# Revit family: Hardware_Glass_Nero
name_source: partatom
category: Specialty Equipment
units: mm (PartAtom-declared; Revit-internal decimal feet)

## family parameters
Always vertical = Yes
Cut with Voids When Loaded = Yes
OmniClass Number = 23.31.25.00
OmniClass Title = Toilet and Bath Specialties
Part Type = Normal
Room Calculation Point = No
Round Connector Dimension = Use Diameter
Shared = No
Work Plane-Based = No

## types (18) — shared parameters
Assembly Code = C1030210
IfcExportAs = IfcFurniture
IfcExportType = NOTDEFINED
Manufacturer = Nero
ManufacturerURLProductSpecific = https://nerotapware.com.au
ModifiedIssue = 20231106 $
URL = https://nerotapware.com.au
Uniclass2015Code = Pr_30_36_36
Uniclass2015Title = Hinges and hanging hardware
Uniclass2015Version = Products v1.28
zero-valued in all types: Default Elevation

## per-type parameters (varying)
| type | 180DegWallToGlassHinge | 90DegWallHinge | 90DegWallToGlassHinge | BodyMaterial | Description | GapBetweenWallandGlass | GlassPanel | GlassToWallHingeF | GlassToWallHingeU | GlassTopHingeF | GrabRail | ManufacturerSpecCode | Model | PerpendicularGlassLeft | PerpendicularWallLeft | PerpendicularWallThickness | RoundShowerKnob | SquareShowerKnob | Type Comments |
| F Shaped Glass to Wall Bracket Brushed Bronze (NRSH202BZ) | Yes | No | No | Metal_Bronze_Nero_Brushed | Shower F Bracket 10mm Glass | 3 mm  [stored 0.00984252 ft] | Yes | Yes | No | No | No | NRSH202BZ | NRSH202BZ | No | Yes | 115 mm  [stored 0.377297 ft] | Yes | No | Bracket - Wall - Shower - F - Brushed Bronze |
| Wall Glass Bracket with 180Deg Door Hinge Brushed Bronze (NRSH204BG+ NRSH102BG+ NRSH301BG) | Yes | Yes | No | Metal_Gold_Nero_Brushed | 90 Degree Glass to Wall Shower Bracket 10mm Glass with 180 Degree Glass to Glass Shower
Hinge 10mm Glass and Round Shower Knob
 and | 0 mm  [stored 0 ft] | Yes | No | No | No | No | NRSH204BG+ NRSH102BG+ NRSH301BG | NRSH204BG+ NRSH102BG+ NRSH301BG | No | Yes | 115 mm  [stored 0.377297 ft] | No | Yes | Bracket - 90Deg Wall Glass - Round Door Knob - Shower - Brushed Gold |
| 90Deg Wall Glass Door Hinge with Grab Rail Brushed Gold (NRSH101BG + NRSH301BG + NRSH303BG) | No | No | Yes | Metal_Gold_Nero_Brushed | 90 Degree Glass to Wall Shower with Shower Hinge 10mm Glass and Knob | 3 mm  [stored 0.00984252 ft] | No | No | No | No | Yes | NRSH101BG+NRSH301BG | NRSH101BG+NRSH301BG | No | Yes | 115 mm  [stored 0.377297 ft] | No | No | Hinge - Wall - Shower - 90Deg - Round Knob - Brushed Gold |
| U Shaped Glass to Wall Bracket Brushed Bronze (NRSH203BZ) | Yes | No | No | Metal_Bronze_Nero_Brushed | Shower U Bracket 10mm Glass | 3 mm  [stored 0.00984252 ft] | Yes | No | Yes | No | No | NRSH203BZ | NRSH203BZ | No | Yes | 115 mm  [stored 0.377297 ft] | No | Yes | Bracket - Wall - Shower - U - Brushed Bronze |
| F Shaped Over Panel Bracket Brushed Bronze (NRSH201BZ) | Yes | No | No | Metal_Bronze_Nero_Brushed | Over-Panel Glass to Glass Fitting 10mm Glass | 3 mm  [stored 0.00984252 ft] | Yes | No | No | Yes | No | NRSH201BZ | NRSH201BZ | Yes | No | 10 mm  [stored 0.0328084 ft] | Yes | No | Hinge - Glass - Over Panel - Brushed Bronze |
| U Shaped Glass Wall Bracket and F Shaped Over Panel Bracket Brushed Bronze (NRSH201BZ + NRSH203BZ) | Yes | No | No | Metal_Bronze_Nero_Brushed | Over-Panel Glass to Glass Fitting 10mm Glass with Shower U Bracket 10mm Glass | 3 mm  [stored 0.00984252 ft] | Yes | No | Yes | Yes | No | NRSH201BZ + NRSH203BZ | NRSH201BZ + NRSH203BZ | Yes | No | 10 mm  [stored 0.0328084 ft] | No | Yes | Bracket - Over Panel F - Wall Glass U - Brushed Bronze |
| Wall Glass Bracket with 180Deg Door Hinge Brushed Bronze (NRSH204BZ+ NRSH102BZ+ NRSH301BZ) | Yes | Yes | No | Metal_Bronze_Nero_Brushed | 90 Degree Glass to Wall Shower Bracket 10mm Glass with 180 Degree Glass to Glass Shower
Hinge 10mm Glass and Round Shower Knob
 and | 0 mm  [stored 0 ft] | Yes | No | No | No | No | NRSH204BZ+ NRSH102BZ+ NRSH301BZ | NRSH204BZ+ NRSH102BZ+ NRSH301BZ | No | Yes | 115 mm  [stored 0.377297 ft] | No | Yes | Bracket - 90Deg - Wall To Glass - Round Door Knob - Shower - Brushed Bronze |
| Wall Glass Bracket with 180Deg Door Hinge Brushed Bronze (NRSH204GM+ NRSH102GM+ NRSH301GM) | Yes | Yes | No | Metal_GunMetal_Nero | 90 Degree Glass to Wall Shower Bracket 10mm Glass with 180 Degree Glass to Glass Shower
Hinge 10mm Glass and Round Shower Knob
 and | 0 mm  [stored 0 ft] | Yes | No | No | No | No | NRSH204GM+ NRSH102GM+ NRSH301GM | NRSH204GM+ NRSH102GM+ NRSH301GM | No | Yes | 115 mm  [stored 0.377297 ft] | No | Yes | Bracket - 90Deg Wall Glass - Round Door Knob - Shower - Gun Metal |
| 90Deg Wall Glass Door Hinge with Grab Rail Brushed Bronze (NRSH101BZ + NRSH301BZ + NRSH303BG) | No | No | Yes | Metal_Bronze_Nero_Brushed | 90 Degree Glass to Wall Shower with Shower Hinge 10mm Glass and Knob | 3 mm  [stored 0.00984252 ft] | No | No | No | No | Yes | NRSH101BZ+NRSH301BZ | NRSH101BZ+NRSH301BZ | No | Yes | 115 mm  [stored 0.377297 ft] | No | No | Hinge - Wall - Shower - 90Deg - Round Knob - Brushed Bronze |
| 90Deg Wall Glass Door Hinge with Grab Rail Gun Metal (NRSH101GM + NRSH301GM + NRSH303GM) | No | No | Yes | Metal_GunMetal_Nero | 90 Degree Glass to Wall Shower with Shower Hinge 10mm Glass and Knob | 3 mm  [stored 0.00984252 ft] | No | No | No | No | Yes | NRSH101GM+NRSH301GM | NRSH101GM+NRSH301GM | No | Yes | 115 mm  [stored 0.377297 ft] | No | No | Hinge - Wall - Shower - 90Deg - Round Knob - Gun Metal |
| F Shaped Over Panel Bracket Brushed Gold (NRSH201BG) | Yes | No | No | Metal_Gold_Nero_Brushed | Over-Panel Glass to Glass Fitting 10mm Glass | 3 mm  [stored 0.00984252 ft] | Yes | No | No | Yes | No | NRSH201BG | NRSH201BG | Yes | No | 10 mm  [stored 0.0328084 ft] | Yes | No | Hinge - Glass - Over Panel - Brushed Gold |
| F Shaped Over Panel Bracket Gun Metal (NRSH201GM) | Yes | No | No | Metal_GunMetal_Nero | Over-Panel Glass to Glass Fitting 10mm Glass | 3 mm  [stored 0.00984252 ft] | Yes | No | No | Yes | No | NRSH201GM | NRSH201GM | Yes | No | 10 mm  [stored 0.0328084 ft] | Yes | No | Hinge - Glass - Over Panel - Gun Metal |
| F Shaped Glass to Wall Hinge Brushed Gold (NRSH202BG) | Yes | No | No | Metal_Gold_Nero_Brushed | Shower F Bracket 10mm Glass | 3 mm  [stored 0.00984252 ft] | Yes | Yes | No | No | No | NRSH202BG | NRSH202BG | No | Yes | 115 mm  [stored 0.377297 ft] | Yes | No | Bracket - Wall - Shower - F - Brushed Gold |
| F Shaped Glass to Wall Bracket Gun Metal (NRSH202GM) | Yes | No | No | Metal_GunMetal_Nero | Shower F Bracket 10mm Glass | 3 mm  [stored 0.00984252 ft] | Yes | Yes | No | No | No | NRSH202GM | NRSH202GM | No | Yes | 115 mm  [stored 0.377297 ft] | Yes | No | Bracket - Wall - Shower - F - Gun Metal |
| U Shaped Glass to Wall Bracket Brushed Gold (NRSH203BG) | Yes | No | No | Metal_Gold_Nero_Brushed | Shower U Bracket 10mm Glass | 3 mm  [stored 0.00984252 ft] | Yes | No | Yes | No | No | NRSH203BG | NRSH203BG | No | Yes | 115 mm  [stored 0.377297 ft] | No | Yes | Bracket - Wall - Shower - U - Brushed Gold |
| U Shaped Glass to Wall Bracket Gun Metal (NRSH203GM) | Yes | No | No | Metal_GunMetal_Nero | Shower U Bracket 10mm Glass | 3 mm  [stored 0.00984252 ft] | Yes | No | Yes | No | No | NRSH203GM | NRSH203GM | No | Yes | 115 mm  [stored 0.377297 ft] | No | Yes | Bracket - Wall - Shower - U - Gun Metal |
| U Shaped Glass Wall Bracket and F Shaped Over Panel Bracket Brushed Gold (NRSH201BG + NRSH203BG) | Yes | No | No | Metal_Gold_Nero_Brushed | Over-Panel Glass to Glass Fitting 10mm Glass with Shower U Bracket 10mm Glass | 3 mm  [stored 0.00984252 ft] | Yes | No | Yes | Yes | No | NRSH201BZ + NRSH203BZ | NRSH201BZ + NRSH203BZ | Yes | No | 10 mm  [stored 0.0328084 ft] | No | Yes | Bracket - Over Panel F - Wall Glass U - Brushed Bronze |
| U Shaped Glass Wall Bracket and F Shaped Over Panel Bracket Gun Metal (NRSH201GM + NRSH203GM) | Yes | No | No | Metal_GunMetal_Nero | Over-Panel Glass to Glass Fitting 10mm Glass with Shower U Bracket 10mm Glass | 3 mm  [stored 0.00984252 ft] | Yes | No | Yes | Yes | No | NRSH201GM + NRSH203GM | NRSH201GM + NRSH203GM | Yes | No | 10 mm  [stored 0.0328084 ft] | No | Yes | Bracket - Over Panel F - Wall Glass U - Gun Metal |

note: [stored X ft] marks values corroborated as IEEE doubles in the binary element streams (Revit-internal decimal feet)

## geometry (parser evidence)
native form markers: Sweep x22
no freeform markers — native parametric forms only
